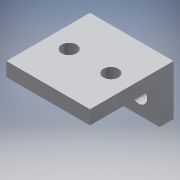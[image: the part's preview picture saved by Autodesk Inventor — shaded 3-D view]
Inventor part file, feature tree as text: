
AUTODESK INVENTOR PART (.ipt)
format: ipt  version: 2017 (Build 210142000, 142)  size: 131,584 bytes
history: native  units: in
note: dims shown in document units (in); Inventor stores cm internally (conversion verified against a paired STEP export)
features: sketch x3, hole x2, projected_geometry x2, extrude x1
ambient origin geometry x8: Origin, YZ Plane, XZ Plane, XY Plane, X Axis, Y Axis, Z Axis, Center Point
bodies: Solid1 (feature_tree)
feature tree (8):
  extrude  "Extrusion1"  Depth=0.75in
  hole  "Hole1"  [1 undecoded]
  hole  "Hole2"  [1 undecoded]
  sketch  "Sketch1"  dims[d0=0.45in d1=0.75in]
  sketch  "Sketch2"  dims[d2=0.325in d3=0.625in]
  projected_geometry  "Projected Loop1"
  sketch  "Sketch3"  dims[d4=0.75in d5=0.0in d6=0.375in d7=0.1875in d8=0.75in d11=0.135in d12=0.75in d13=0.375in d14=0.25in d15=0.5635in d16=1.0in d17=0.8108in d20=0.375in d21=0.1875in d22=0.1625in d23=0.1625in d24=0.15in d25=0.75in d26=0.375in d27=0.25in d28=0.5635in d29=1.0in d30=0.8108in d31=0.75in d32=0.75in d33=0.325in d34=0.25in d35=0.25in]
  projected_geometry  "Projected Loop2"
note: 2 required parameter values undecoded (feature->parameter linkage not recoverable at this tier; creation-order binding heuristic only, values carry confidence <= 0.55)
